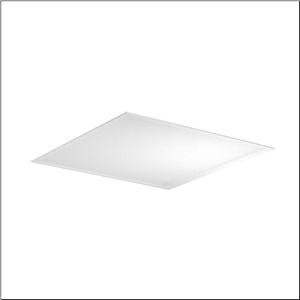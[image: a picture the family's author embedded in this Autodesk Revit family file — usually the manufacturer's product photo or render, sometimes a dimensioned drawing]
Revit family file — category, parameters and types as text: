
# Revit family: apollon_r__31_square_51mp12wd2m42_b676
name_source: partatom
category: Lighting Fixtures
units: mm (PartAtom-declared; Revit-internal decimal feet)

## family parameters
Cut with Voids When Loaded = No
Host = Face
Light Source = No
Part Type = Normal
Room Calculation Point = No
Round Connector Dimension = Use Diameter
Shared = No

## types (1)
- --- (1 x LED, 4000 lm, 27.5 W, 4000K)
    Apparent Load = 28 VA
    CIE Flux Codes = 62 87 97 100 100
    Color Rendering = 80
    Color Temperature = 4000K
    Default Elevation = 1800 mm
    Description = Apollon® 31 square, office luminaire, primary optical cover: micro prismatic cover, of PMMA, CAT 2 (L<= 3000cd/m²), light emission: direct distribution, primary light characteristic: symmetric, installation type: lay-in mounting, LED, rated luminous flux: 4.000lm, luminous efficacy: 142lm/W, light colour: 830/840, colour temperature: 3000/4000K, with terminal, 5-pole, mains connection: 220..240V, AC/DC, 0/50..60Hz, rated input power: 28W, housing, of aluminium, traffic white (RAL 9016), module: M600, length: 595mm, width: 595mm, height: 32mm, housing upper side, of sheet steel, galvanised, protection rating (complete): IP20, protection rating (on room side): IP40, insulation class (complete): insulation class II (safety insulation), certification: CE, ENEC, impact resistance: IK03, permissible operating ambient temperature: -20..+40°C, permissible storage temperature: -20..+60°C, packaging unit: 1 piece
    Height = 0 mm  [stored 0 ft]
    Lamp = 1 x LED
    Lamp Light Flux = 4000 lm
    Lamp Power = 27.5 W
    Lamp count = 1
    Length = 595 mm
    Luminous efficacy = 145 lm/W
    Manufacturer = Siteco
    ModVariant = No
    Model = 51MP12WD2M42
    Mounting Place = Ceiling
    Mounting Type = Recessed
    Number of Poles = 1
    OnlyDefault = Yes
    Power Factor = 1
    Product Name = Apollon® 31 square
    Product group = office luminaire | ceiling recessed
    ProductGroupID = 401
    Protection Class = Protection class II
    Protection Degree = IP 20
    RLX_Detail_Level = 1
    RLX_Emergency_Light_Flux = 0 lm
    RLX_Emergency_Type = 0
    RLX_Emergency_Type_DB = No
    RlxData = <blob elided: 12725 chars, md5=a962938e>
    Socket = socket
    Standby Power = 0 W
    System Light Flux = 4000 lm
    System Power = 28 W
    Type Comments = factory setting: colour temperature 4000K
    Type Image = l_1291035.jpg
    URL = http://relux.com
    VarID = @adj_027781
    Voltage = 0 V
    Weight = 0.00 kg
    Width = 595 mm

note: [stored X ft] marks values corroborated as IEEE doubles in the binary element streams (Revit-internal decimal feet)

## geometry (parser evidence)
native form markers: Sweep x9
no freeform markers — native parametric forms only
